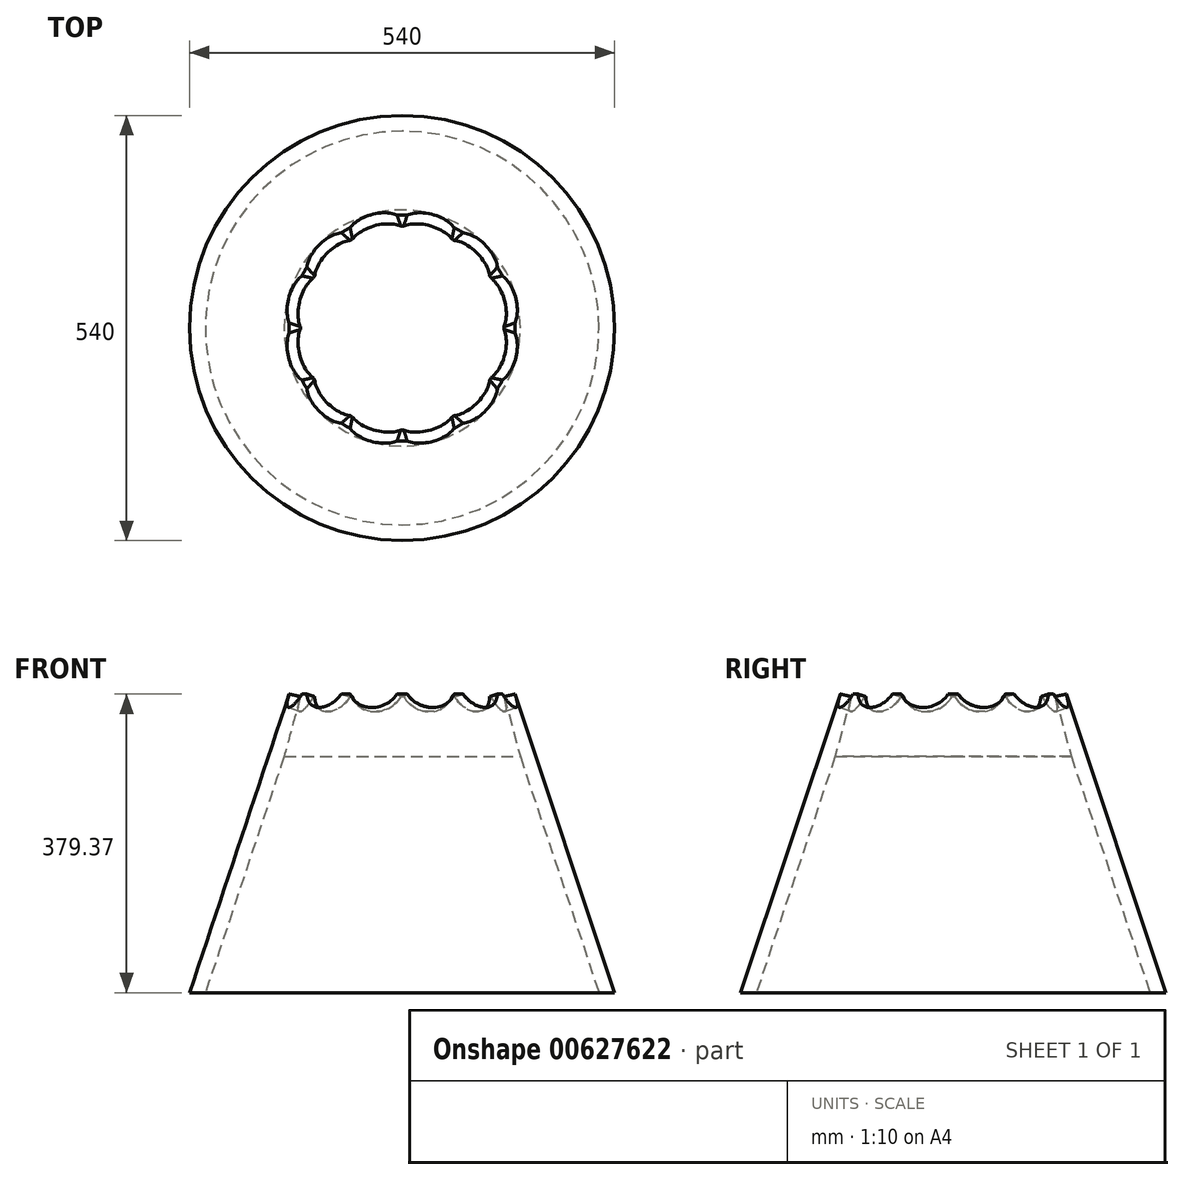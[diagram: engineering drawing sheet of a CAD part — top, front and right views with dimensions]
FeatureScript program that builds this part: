
annotation { "Feature Type Name" : "Feature", "Feature Type Description" : "" }
export const myFeature = defineFeature(function(context is Context, id is Id, definition is map)
    precondition{}
    {
        {
            var Q0;
            Q0=qCreatedBy(makeId("Front.planeOp"),FACE);
            var sketch = newSketch(context, id + "F0", { "sketchPlane" : qUnion([Q0])});
            skLineSegment(sketch, "E0", {"start": v(-150, 300) * mm, "end": v(-250, 0) * mm});
            skLineSegment(sketch, "E1", {"start": v(-250, 0) * mm, "end": v(-270, 0) * mm});
            skLineSegment(sketch, "E2", {"start": v(-270, 0) * mm, "end": v(-143.5, 379.47) * mm});
            skLineSegment(sketch, "E3", {"start": v(-143.5, 379.47) * mm, "end": v(-128.5, 379.47) * mm});
            skLineSegment(sketch, "E4", {"start": v(-128.5, 379.47) * mm, "end": v(-150, 300) * mm});
            skSolve(sketch);
        }
        {
            var Q0;
            Q0=qCreatedBy(makeId("Front.planeOp"),FACE);
            var sketch = newSketch(context, id + "F1", { "sketchPlane" : qUnion([Q0])});
            skLineSegment(sketch, "E5", {"start": v(0, 0) * mm, "end": v(0, 307.68) * mm});
            skSolve(sketch);
        }
        {
            var Q0;
            Q0=makeQuery(id+"F0.imprint","IMPRINT",FACE,{"disambiguationData":[TD([[makeQuery(id+"F0.imprint","IMPRINT",EDGE,{"derivedFrom":sQuery(id+"F0.wireOp",EDGE,"E0")}),-1.0]])]});
            var Q1;
            Q1=sQuery(id+"F1.wireOp",EDGE,"E5");
            revolve(context, id + "F2", {"entities" : qUnion([Q0]), "axis" : qUnion([Q1]), "revolveType" : RevolveType.ONE_DIRECTION, "angle" : 30 * degree});
        }
        {
            var Q0;
            Q0 = qBodyType(qCreatedBy(id + "F1" ,EDGE), BodyType.WIRE);
            var Q1;
            Q1=qCreatedBy(id+"F4.planeOp",FACE);
            cPlane(context, id + "F3", {"entities" : qUnion([Q0, Q1]), "cplaneType" : CPlaneType.LINE_ANGLE, "offset" : 25 * mm, "angle" : 15 * degree, "width" : 150 * mm, "height" : 150 * mm});
        }
        {
            var Q0;
            Q0=qCreatedBy(id+"F3.planeOp",FACE);
            cPlane(context, id + "F4", {"entities" : qUnion([Q0]), "cplaneType" : CPlaneType.OFFSET, "offset" : 150 * mm, "oppositeDirection" : true, "width" : 150 * mm, "height" : 150 * mm});
        }
        {
            var Q0;
            Q0=qCreatedBy(id+"F4.planeOp",FACE);
            var sketch = newSketch(context, id + "F5", { "sketchPlane" : qUnion([Q0])});
            skLineSegment(sketch, "E6", {"start": v(123.35, 350) * mm, "end": v(-129.89, 350) * mm});
            skSolve(sketch);
        }
        {
            var Q0;
            Q0=qCreatedBy(id+"F4.planeOp",FACE);
            var Q1;
            Q1 = qBodyType(qCreatedBy(id + "F5" ,EDGE), BodyType.WIRE);
            cPlane(context, id + "F6", {"entities" : qUnion([Q0, Q1]), "cplaneType" : CPlaneType.LINE_ANGLE, "offset" : 25 * mm, "angle" : 20 * degree, "oppositeDirection" : true, "width" : 150 * mm, "height" : 150 * mm});
        }
        {
            var Q0;
            Q0=qCreatedBy(id+"F6.planeOp",FACE);
            var sketch = newSketch(context, id + "F7", { "sketchPlane" : qUnion([Q0])});
            skPoint(sketch, "E7", {"position": v(-59.64, 305.65) * mm});
            skPoint(sketch, "E8", {"position": v(3.12, 311.56) * mm});
            skCircle(sketch, "E9", {"center": v(-29.57, 322.56) * mm, "radius": 34.5 * mm});
            skPoint(sketch, "E9.third.point", {"position": v(-25.12, 288.35) * mm});
            skSolve(sketch);
        }
        {
            var Q0;
            Q0 = qSketchRegion(id + "F7", true);
            extrude(context, id + "F8", {"entities" : qUnion([Q0]), "operationType" : NewBodyOperationType.REMOVE, "endBound" : BoundingType.SYMMETRIC, "oppositeDirection" : true, "depth" : 100 * mm, "offsetDistance" : 25 * mm});
        }
        {
            var Q0;
            Q0=makeQuery(id+"F2.opRevolve","SWEPT_BODY",BODY,{"disambiguationData":[OSD([sQuery(id+"F0.wireOp",EDGE,"E0"),sQuery(id+"F0.wireOp",EDGE,"E1"),sQuery(id+"F0.wireOp",EDGE,"fKRv1d6K-o61f-OzIg-PQ9P-X68rh1wgNbdu"),sQuery(id+"F0.wireOp",EDGE,"HxRSdhod-90rD-GvnV-GXxi-EBpZglpgOxL8"),sQuery(id+"F0.wireOp",EDGE,"Xlw2WM3j-V6UL-staa-xDYz-mzKcfrXvtrXq")])]});
            var Q1;
            Q1=sQuery(id+"F1.wireOp",EDGE,"E5");
            circularPattern(context, id + "F9", {"operationType" : NewBodyOperationType.ADD, "entities" : qUnion([Q0]), "axis" : qUnion([Q1]), "angle" : 360 * degree, "instanceCount" : 12, "equalSpace" : true});
        }
        {
            var Q0;
            Q0=qCreatedBy(makeId("Front.planeOp"),FACE);
            var sketch = newSketch(context, id + "F10", { "sketchPlane" : qUnion([Q0])});
            skLineSegment(sketch, "E10", {"start": v(-88.86, 366.89) * mm, "end": v(-68.6, 451.64) * mm});
            skLineSegment(sketch, "E11", {"start": v(-68.6, 451.64) * mm, "end": v(-222.9, 443.21) * mm});
            skLineSegment(sketch, "E12", {"start": v(-88.86, 366.89) * mm, "end": v(-155.57, 382.11) * mm});
            skLineSegment(sketch, "E13", {"start": v(-155.57, 382.11) * mm, "end": v(-222.9, 443.21) * mm});
            skSolve(sketch);
        }
        {
            var Q0;
            Q0=makeQuery(id+"F10.imprint","IMPRINT",FACE,{"disambiguationData":[TD([[makeQuery(id+"F10.imprint","IMPRINT",EDGE,{"derivedFrom":sQuery(id+"F10.wireOp",EDGE,"E10")}),1.0]])]});
            var Q1;
            Q1=sQuery(id+"F1.wireOp",EDGE,"E5");
            revolve(context, id + "F11", {"operationType" : NewBodyOperationType.REMOVE, "entities" : qUnion([Q0]), "axis" : qUnion([Q1]), "revolveType" : RevolveType.FULL, "oppositeDirection" : true});
        }
    });
